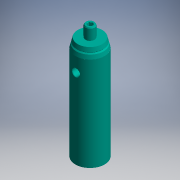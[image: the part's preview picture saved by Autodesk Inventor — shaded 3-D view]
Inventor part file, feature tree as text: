
AUTODESK INVENTOR PART (.ipt)
format: ipt  version: 2016 (Build 200138000, 138)  size: 220,160 bytes
history: native  units: mm (DEFAULTED — no unit token found)
features: other x2, extrude x1, sketch x1
ambient origin geometry x8: Origin, YZ Plane, XZ Plane, XY Plane, X Axis, Y Axis, Z Axis, Center Point
bodies: Solid1 (feature_tree), Solid2 (feature_tree)
feature tree (4):
  extrude  "Extrusion1"  [1 undecoded]
  sketch  "Sketch1"  dims[d0=5.2mm d1=0.0mm]
  other  "0331-001-1-solid1"
  other  "21110-001-1-solid1"
note: 1 required parameter value undecoded (feature->parameter linkage not recoverable at this tier; creation-order binding heuristic only, values carry confidence <= 0.55)
